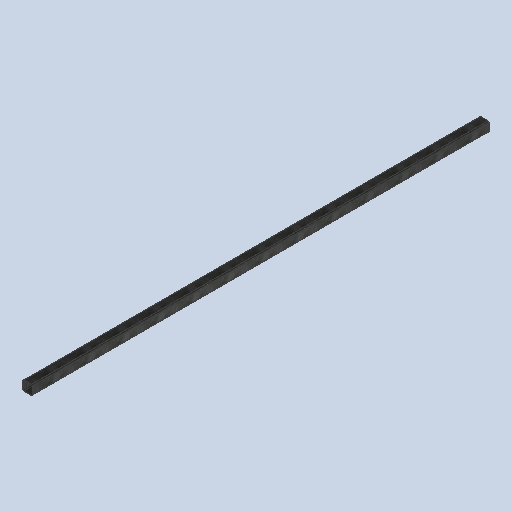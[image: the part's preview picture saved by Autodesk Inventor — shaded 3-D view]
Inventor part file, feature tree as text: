
AUTODESK INVENTOR PART (.ipt)
format: ipt  version: 2025 (Build 290162010, 162A)  size: 117,248 bytes
history: native  units: mm
features: other x1, extrude x1, sketch x1
ambient origin geometry x8: Origin, YZ Plane, XZ Plane, XY Plane, X Axis, Y Axis, Z Axis, Center Point
bodies: Solid1 (feature_tree)
feature tree (3):
  other  "BSH 065 tube 5"
  extrude  "Extrusion1"  Depth=6.0mm
  sketch  "Sketch1"  dims[d0=6.0mm d1=50.0mm d2=50.0mm d3=2.0mm d6=6.0mm d7=100.0mm d8=100.0mm d9=3.0mm d10=2300.0mm d11=0.0mm]
